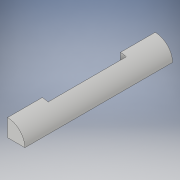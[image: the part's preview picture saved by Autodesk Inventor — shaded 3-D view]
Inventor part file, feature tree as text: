
AUTODESK INVENTOR PART (.ipt)
format: ipt  version: 2019.1 (Build 231200000, 200)  size: 109,056 bytes
history: native  units: in
note: dims shown in document units (in); Inventor stores cm internally (conversion verified against a paired STEP export)
features: extrude x2, sketch x2
ambient origin geometry x8: Origin, YZ Plane, XZ Plane, XY Plane, X Axis, Y Axis, Z Axis, Center Point
bodies: Solid1 (feature_tree)
feature tree (4):
  extrude  "Extrusion1"  Depth=6.375in TaperAngle=0.0deg
  extrude  "Extrusion2"  Depth=1.5in
  sketch  "Sketch1"  dims[d0=1.5in d1=6.375in d2=0.0in]
  sketch  "Sketch2"  dims[d3=3.375in d4=1.5in d5=0.25in d6=0.0in d7=0.0in]
